# Revit family: Hekatron_Feststellanlagen_K THM-01_DE_22.01
name_source: partatom
category: Brandmelder
revit_build: Autodesk Revit 2018 (Build: 20190510_1515(x64)
units: mm (PartAtom-declared; Revit-internal decimal feet)

## family parameters
Basisbauteil = Fläche
Beim Laden mit Abzugskörper schneiden = Nein
Bemaßung runder Anschluss = Durchmesser verwenden
Beschriftungsausrichtung beibehalten = Ja
Gemeinsam genutzt = Nein
OmniClass-Nummer = 23.85.30.21
OmniClass-Titel = Environmental Detection/Registration
Raumberechnungspunkt = Nein
Teiletyp = Normal

## types (1)
- K THM-01
    Beschreibung = Konsole zur Boden- und Wandmontage von Türhaftmagneten. Passend für die Türhaftmagnete THM 425, THM 425-1, THM 433, THM 433-1, THM 440 bis THM 444, THM 446 und THM 447.
    Breite (mm) = 80.0
    Farbe = lichtgrau
    Hersteller = Hekatron
    Höhe (mm) = 140.0
    Link zu Ausschreibungstext = https://www.meinhplus.de
    Link zu ausschreiben.de = http://www.ausschreiben.de
    Material = Stahlblech
    Modell = K THM-01
    Montageart = Aufputz
    Tiefe (mm) = 95.0
    Typenkommentare = Konsole für Türhaftmagnete
    UB A&S Artikel Nummer = 31-6800000-01-01
    URL = https://www.hekatron-brandschutz.de
    Version des BIM Objektes = 22.01
    Vorgabe-Ansicht = 1200 mm

## geometry (parser evidence)
native form markers: Sweep x2
no freeform markers — native parametric forms only
